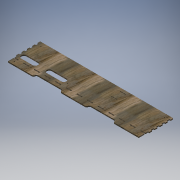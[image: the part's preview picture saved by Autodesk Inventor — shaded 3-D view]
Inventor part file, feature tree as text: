
AUTODESK INVENTOR PART (.ipt)
format: ipt  version: 2018.3 (Build 223284000, 284)  size: 3,303,936 bytes
history: native  units: mm
features: reference x20, other x8, extrude x5, sketch x5
ambient origin geometry x8: Origin, YZ Plane, XZ Plane, XY Plane, X Axis, Y Axis, Z Axis, Center Point
bodies: Solido1 (feature_tree)
feature tree (38):
  extrude  "Estrusione1"  Depth=95.0mm
  extrude  "Estrusione2"  TaperAngle=90.0deg  [1 undecoded]
  extrude  "Estrusione3"  Depth=95.0mm
  extrude  "Estrusione4"  Depth=5.0mm
  extrude  "Estrusione5"  Depth=90.0mm
  sketch  "Schizzo1"
  reference  "Riferimento1"
  reference  "Riferimento2"
  reference  "Riferimento3"
  reference  "Riferimento4"
  reference  "Riferimento5"
  reference  "Riferimento6"
  reference  "Riferimento7"
  reference  "Riferimento8"
  reference  "Riferimento9"
  reference  "Riferimento10"
  reference  "Riferimento11"
  reference  "Riferimento12"
  reference  "Riferimento13"
  sketch  "Schizzo2"
  reference  "Riferimento14"
  reference  "Riferimento15"
  reference  "Riferimento16"
  reference  "Riferimento17"
  sketch  "Schizzo3"
  reference  "Riferimento18"
  reference  "Riferimento19"
  reference  "Riferimento20"
  sketch  "Schizzo5"
  other  "Linea chiusa proiettata1"
  sketch  "Schizzo6"
  other  "Immagine1"
  other  "Immagine2"
  other  "<userpath>\Desktop\Scorbot Hardware\Case Board V2\caseHw v2.iam"
  other  "caseHw v2.iam"
  other  "tavolaBase:1"
  other  "LatoAlimentatore:1"
  other  "LatoPy:1"
note: 1 required parameter value undecoded (feature->parameter linkage not recoverable at this tier; creation-order binding heuristic only, values carry confidence <= 0.55)
